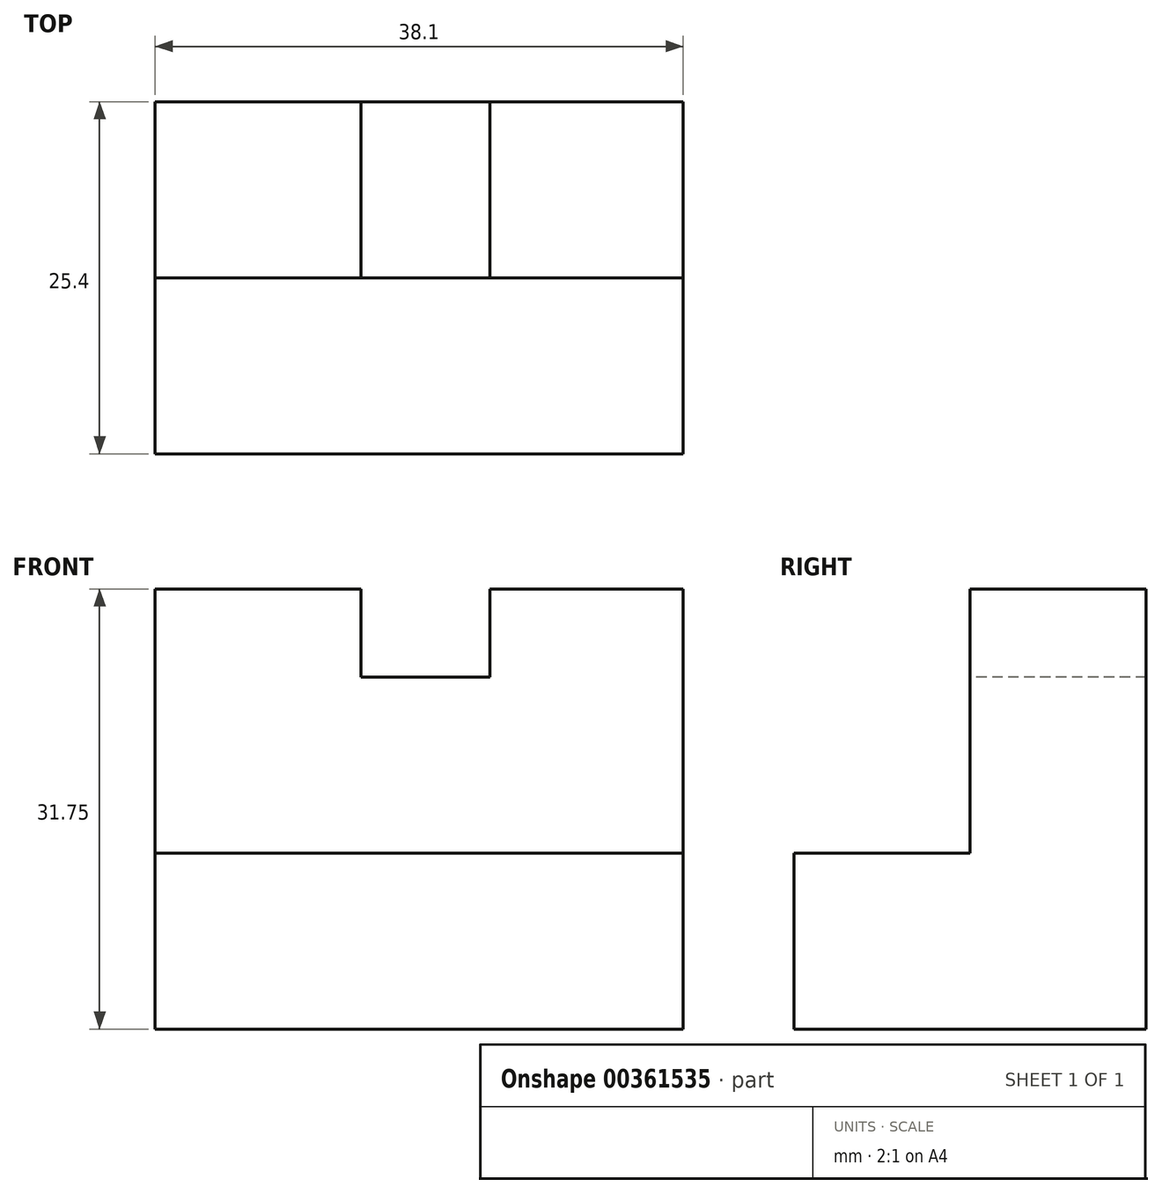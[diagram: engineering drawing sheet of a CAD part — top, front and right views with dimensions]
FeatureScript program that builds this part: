
annotation { "Feature Type Name" : "Feature", "Feature Type Description" : "" }
export const myFeature = defineFeature(function(context is Context, id is Id, definition is map)
    precondition{}
    {
        {
            var Q0;
            Q0=qCreatedBy(makeId("Right.planeOp"),FACE);
            var sketch = newSketch(context, id + "F0", { "sketchPlane" : qUnion([Q0])});
            skLineSegment(sketch, "E0", {"start": v(0, 31.75) * mm, "end": v(0, 0) * mm});
            skLineSegment(sketch, "E1", {"start": v(0, 0) * mm, "end": v(-25.4, 0) * mm});
            skLineSegment(sketch, "E2", {"start": v(-25.4, 0) * mm, "end": v(-25.4, 12.7) * mm});
            skLineSegment(sketch, "E3", {"start": v(-25.4, 12.7) * mm, "end": v(-12.7, 12.7) * mm});
            skLineSegment(sketch, "E4", {"start": v(-12.7, 12.7) * mm, "end": v(-12.7, 31.75) * mm});
            skLineSegment(sketch, "E5", {"start": v(-12.7, 31.75) * mm, "end": v(0, 31.75) * mm});
            skSolve(sketch);
        }
        {
            var Q0;
            Q0=makeQuery(id+"F0.imprint","IMPRINT",FACE,{"disambiguationData":[TD([[makeQuery(id+"F0.imprint","IMPRINT",EDGE,{"derivedFrom":sQuery(id+"F0.wireOp",EDGE,"E0")}),-1.0]])]});
            extrude(context, id + "F1", {"entities" : qUnion([Q0]), "depth" : 38.1 * mm});
        }
        {
            var Q0;
            Q0=makeQuery(id+"F1.opExtrude","SWEPT_FACE",FACE,{"disambiguationData":[OSD([sQuery(id+"F0.wireOp",EDGE,"E5")])]});
            var sketch = newSketch(context, id + "F2", { "sketchPlane" : qUnion([Q0])});
            skLineSegment(sketch, "E6", {"start": v(14.86, 0) * mm, "end": v(14.86, -12.7) * mm});
            skPoint(sketch, "E7", {"position": v(19.05, -12.7) * mm});
            skLineSegment(sketch, "E8", {"start": v(24.14, 0) * mm, "end": v(24.14, -12.7) * mm});
            skLineSegment(sketch, "E9", {"start": v(14.86, 0) * mm, "end": v(24.14, 0) * mm});
            skLineSegment(sketch, "E10", {"start": v(14.86, -12.7) * mm, "end": v(24.14, -12.7) * mm});
            skSolve(sketch);
        }
        {
            var Q0;
            Q0=makeQuery(id+"F2.imprint","IMPRINT",FACE,{"disambiguationData":[TD([[makeQuery(id+"F2.imprint","IMPRINT",EDGE,{"derivedFrom":sQuery(id+"F2.wireOp",EDGE,"E6")}),1.0]])]});
            extrude(context, id + "F3", {"entities" : qUnion([Q0]), "operationType" : NewBodyOperationType.REMOVE, "oppositeDirection" : true, "depth" : 6.35 * mm});
        }
    });
